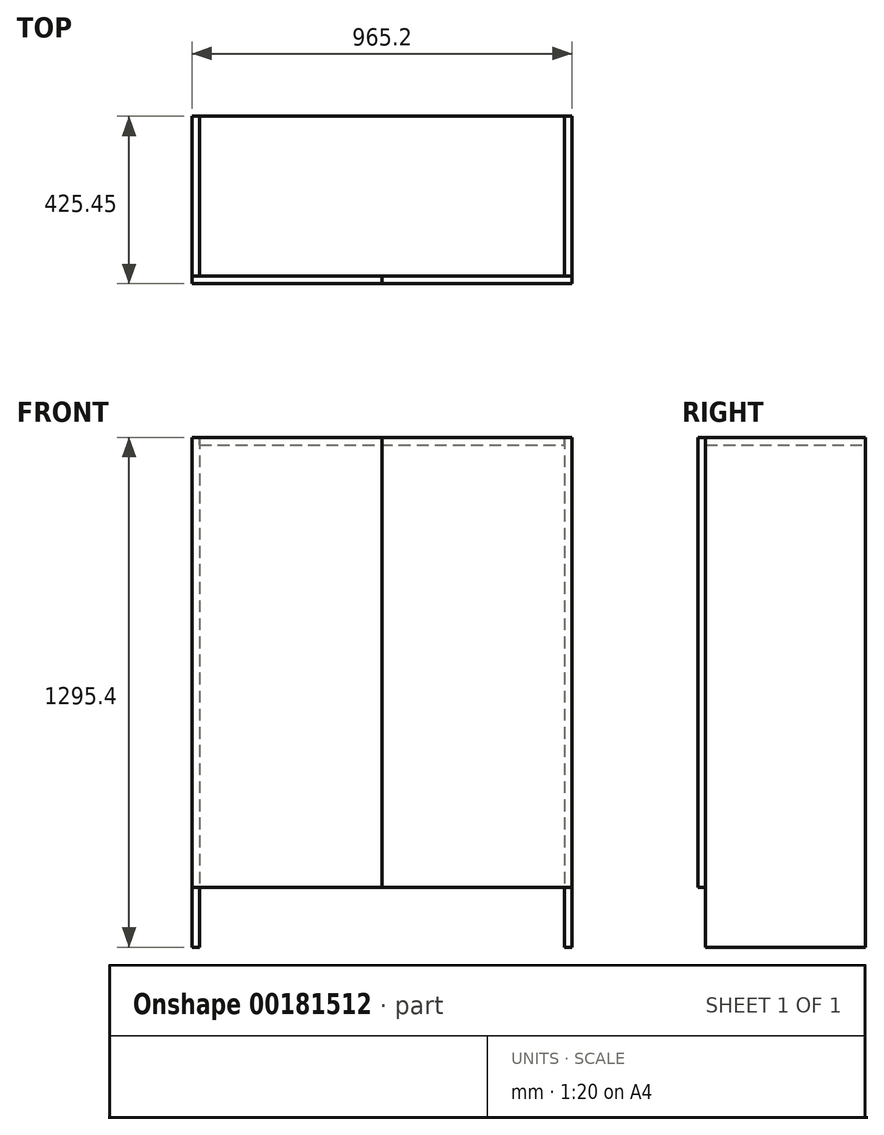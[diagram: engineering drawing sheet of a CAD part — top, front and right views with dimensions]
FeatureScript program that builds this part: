
annotation { "Feature Type Name" : "Feature", "Feature Type Description" : "" }
export const myFeature = defineFeature(function(context is Context, id is Id, definition is map)
    precondition{}
    {
        {
            var Q0;
            Q0=qCreatedBy(makeId("Top.planeOp"),FACE);
            var sketch = newSketch(context, id + "F0", { "sketchPlane" : qUnion([Q0])});
            skLineSegment(sketch, "E0.bottom", {"start": v(0, 0) * mm, "end": v(19.05, 0) * mm});
            skLineSegment(sketch, "E0.top", {"start": v(0, 406.4) * mm, "end": v(19.05, 406.4) * mm});
            skLineSegment(sketch, "E0.left", {"start": v(0, 0) * mm, "end": v(0, 406.4) * mm});
            skLineSegment(sketch, "E0.right", {"start": v(19.05, 0) * mm, "end": v(19.05, 406.4) * mm});
            skSolve(sketch);
        }
        {
            var Q0;
            Q0=qCreatedBy(makeId("Top.planeOp"),FACE);
            cPlane(context, id + "F1", {"entities" : qUnion([Q0]), "cplaneType" : CPlaneType.OFFSET, "offset" : 152.4 * mm, "width" : 152.4 * mm, "height" : 152.4 * mm});
        }
        {
            var Q0;
            Q0=qCreatedBy(makeId("Top.planeOp"),FACE);
            cPlane(context, id + "F2", {"entities" : qUnion([Q0]), "cplaneType" : CPlaneType.OFFSET, "offset" : 1295.4 * mm, "width" : 152.4 * mm, "height" : 152.4 * mm});
        }
        {
            var Q0;
            Q0 = qSketchRegion(id + "F0", true);
            extrude(context, id + "F3", {"entities" : qUnion([Q0]), "depth" : 1295.4 * mm});
        }
        {
            var Q0;
            Q0=qCreatedBy(id+"F1.planeOp",FACE);
            var sketch = newSketch(context, id + "F4", { "sketchPlane" : qUnion([Q0])});
            skLineSegment(sketch, "E1.bottom", {"start": v(19.05, 0) * mm, "end": v(946.15, 0) * mm});
            skLineSegment(sketch, "E1.top", {"start": v(19.05, 406.4) * mm, "end": v(946.15, 406.4) * mm});
            skLineSegment(sketch, "E1.left", {"start": v(19.05, 0) * mm, "end": v(19.05, 406.4) * mm});
            skLineSegment(sketch, "E1.right", {"start": v(946.15, 0) * mm, "end": v(946.15, 406.4) * mm});
            skSolve(sketch);
        }
        {
            var Q0;
            Q0=qCreatedBy(makeId("Top.planeOp"),FACE);
            var sketch = newSketch(context, id + "F5", { "sketchPlane" : qUnion([Q0])});
            skLineSegment(sketch, "E2.bottom", {"start": v(946.15, 0) * mm, "end": v(965.2, 0) * mm});
            skLineSegment(sketch, "E2.top", {"start": v(946.15, 406.4) * mm, "end": v(965.2, 406.4) * mm});
            skLineSegment(sketch, "E2.left", {"start": v(946.15, 0) * mm, "end": v(946.15, 406.4) * mm});
            skLineSegment(sketch, "E2.right", {"start": v(965.2, 0) * mm, "end": v(965.2, 406.4) * mm});
            skSolve(sketch);
        }
        {
            var Q0;
            Q0 = qSketchRegion(id + "F5", true);
            extrude(context, id + "F6", {"entities" : qUnion([Q0]), "operationType" : NewBodyOperationType.ADD, "depth" : 1295.4 * mm});
        }
        {
            var Q0;
            Q0=qCreatedBy(id+"F2.planeOp",FACE);
            var sketch = newSketch(context, id + "F7", { "sketchPlane" : qUnion([Q0])});
            skLineSegment(sketch, "E3.bottom", {"start": v(19.05, 0) * mm, "end": v(946.15, 0) * mm});
            skLineSegment(sketch, "E3.top", {"start": v(19.05, 406.4) * mm, "end": v(946.15, 406.4) * mm});
            skLineSegment(sketch, "E3.left", {"start": v(19.05, 0) * mm, "end": v(19.05, 406.4) * mm});
            skLineSegment(sketch, "E3.right", {"start": v(946.15, 0) * mm, "end": v(946.15, 406.4) * mm});
            skSolve(sketch);
        }
        {
            var Q0;
            Q0=makeQuery(id+"F7.imprint","IMPRINT",FACE,{"disambiguationData":[TD([[makeQuery(id+"F7.imprint","IMPRINT",EDGE,{"derivedFrom":sQuery(id+"F7.wireOp",EDGE,"E3.bottom")}),1.0]])]});
            extrude(context, id + "F8", {"entities" : qUnion([Q0]), "oppositeDirection" : true, "depth" : 19.05 * mm});
        }
        {
            var Q0;
            Q0=qCreatedBy(id+"F1.planeOp",FACE);
            var sketch = newSketch(context, id + "F9", { "sketchPlane" : qUnion([Q0])});
            skLineSegment(sketch, "E4.bottom", {"start": v(0, 0) * mm, "end": v(482.6, 0) * mm});
            skLineSegment(sketch, "E4.top", {"start": v(0, -19.05) * mm, "end": v(482.6, -19.05) * mm});
            skLineSegment(sketch, "E4.left", {"start": v(0, 0) * mm, "end": v(0, -19.05) * mm});
            skLineSegment(sketch, "E4.right", {"start": v(482.6, 0) * mm, "end": v(482.6, -19.05) * mm});
            skLineSegment(sketch, "E5.bottom", {"start": v(965.2, 0) * mm, "end": v(482.6, 0) * mm});
            skLineSegment(sketch, "E5.top", {"start": v(965.2, -19.05) * mm, "end": v(482.6, -19.05) * mm});
            skLineSegment(sketch, "E5.left", {"start": v(965.2, 0) * mm, "end": v(965.2, -19.05) * mm});
            skSolve(sketch);
        }
        {
            var Q0;
            Q0=makeQuery(id+"F9.imprint","IMPRINT",FACE,{"disambiguationData":[TD([[makeQuery(id+"F9.imprint","IMPRINT",EDGE,{"derivedFrom":sQuery(id+"F9.wireOp",EDGE,"E4.bottom")}),-1.0]])]});
            extrude(context, id + "F10", {"entities" : qUnion([Q0]), "depth" : 1143 * mm});
        }
        {
            var Q0;
            Q0=makeQuery(id+"F9.imprint","IMPRINT",FACE,{"disambiguationData":[TD([[makeQuery(id+"F9.imprint","IMPRINT",EDGE,{"derivedFrom":sQuery(id+"F9.wireOp",EDGE,"E5.bottom")}),1.0]])]});
            extrude(context, id + "F11", {"entities" : qUnion([Q0]), "depth" : 1143 * mm});
        }
    });
